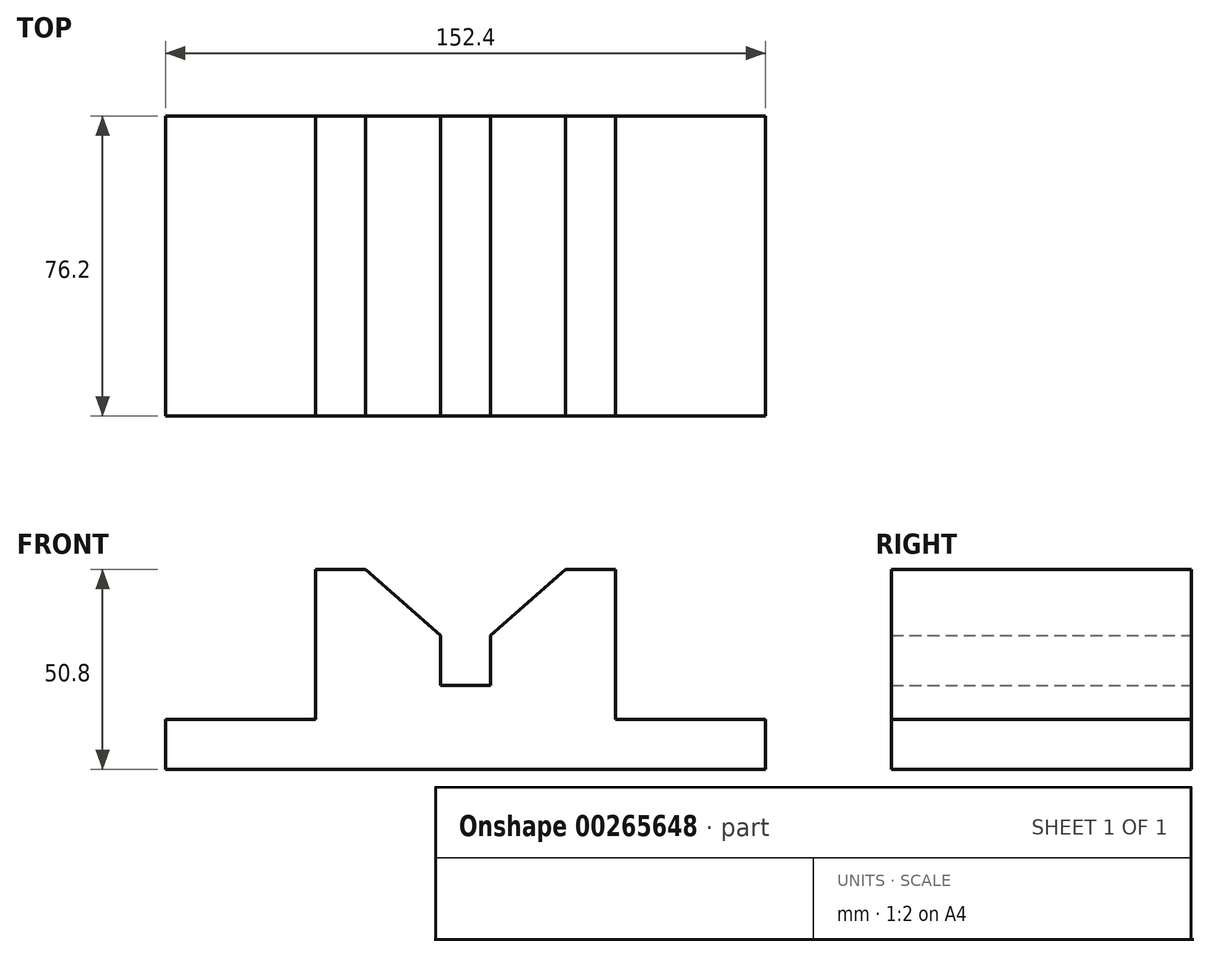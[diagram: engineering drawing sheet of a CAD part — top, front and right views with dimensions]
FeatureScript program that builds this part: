
annotation { "Feature Type Name" : "Feature", "Feature Type Description" : "" }
export const myFeature = defineFeature(function(context is Context, id is Id, definition is map)
    precondition{}
    {
        {
            var Q0;
            Q0=qCreatedBy(makeId("Front.planeOp"),FACE);
            var sketch = newSketch(context, id + "F0", { "sketchPlane" : qUnion([Q0])});
            skLineSegment(sketch, "E0", {"start": v(-38.1, 0) * mm, "end": v(114.3, 0) * mm});
            skLineSegment(sketch, "E1", {"start": v(-38.1, 0) * mm, "end": v(-38.1, 12.7) * mm});
            skLineSegment(sketch, "E2", {"start": v(114.3, 0) * mm, "end": v(114.3, 12.7) * mm});
            skLineSegment(sketch, "E3", {"start": v(-38.1, 12.7) * mm, "end": v(0, 12.7) * mm});
            skLineSegment(sketch, "E4", {"start": v(0, 12.7) * mm, "end": v(0, 50.8) * mm});
            skLineSegment(sketch, "E5", {"start": v(0, 50.8) * mm, "end": v(12.7, 50.8) * mm});
            skLineSegment(sketch, "E6", {"start": v(12.7, 50.8) * mm, "end": v(31.75, 34) * mm});
            skLineSegment(sketch, "E7", {"start": v(31.75, 34) * mm, "end": v(31.75, 21.3) * mm});
            skLineSegment(sketch, "E8", {"start": v(31.75, 21.3) * mm, "end": v(44.45, 21.3) * mm});
            skLineSegment(sketch, "E9", {"start": v(44.45, 21.3) * mm, "end": v(44.45, 34) * mm});
            skLineSegment(sketch, "E10", {"start": v(114.3, 12.7) * mm, "end": v(76.2, 12.7) * mm});
            skLineSegment(sketch, "E11", {"start": v(76.2, 12.7) * mm, "end": v(76.2, 50.8) * mm});
            skLineSegment(sketch, "E12", {"start": v(76.2, 50.8) * mm, "end": v(63.5, 50.8) * mm});
            skLineSegment(sketch, "E13", {"start": v(63.5, 50.8) * mm, "end": v(44.45, 34) * mm});
            skSolve(sketch);
        }
        {
            var Q0;
            Q0 = qSketchRegion(id + "F0", true);
            extrude(context, id + "F1", {"entities" : qUnion([Q0]), "depth" : 76.2 * mm});
        }
    });
